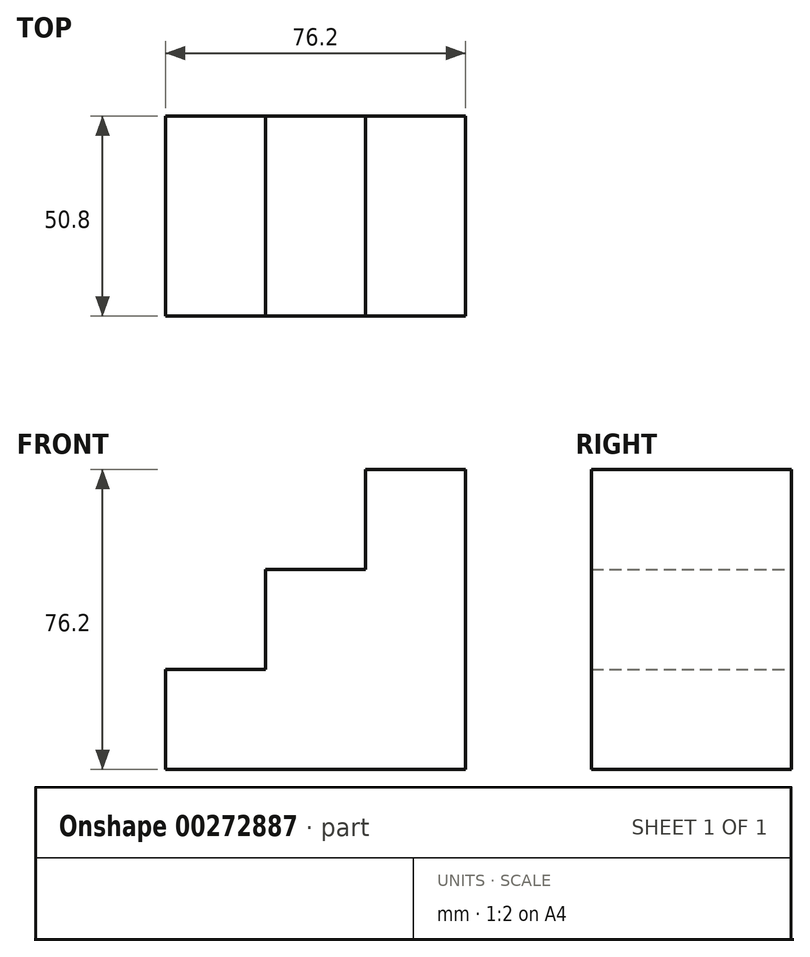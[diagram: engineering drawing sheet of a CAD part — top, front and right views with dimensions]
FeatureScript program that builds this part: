
annotation { "Feature Type Name" : "Feature", "Feature Type Description" : "" }
export const myFeature = defineFeature(function(context is Context, id is Id, definition is map)
    precondition{}
    {
        {
            var Q0;
            Q0=qCreatedBy(makeId("Front.planeOp"),FACE);
            var sketch = newSketch(context, id + "F0", { "sketchPlane" : qUnion([Q0])});
            skLineSegment(sketch, "E0", {"start": v(0, 0) * mm, "end": v(0, 76.2) * mm});
            skLineSegment(sketch, "E1", {"start": v(0, 76.2) * mm, "end": v(-25.4, 76.2) * mm});
            skLineSegment(sketch, "E2", {"start": v(-25.4, 76.2) * mm, "end": v(-25.4, 50.8) * mm});
            skLineSegment(sketch, "E3", {"start": v(-25.4, 50.8) * mm, "end": v(-50.8, 50.8) * mm});
            skLineSegment(sketch, "E4", {"start": v(-50.8, 50.8) * mm, "end": v(-50.8, 25.4) * mm});
            skLineSegment(sketch, "E5", {"start": v(-50.8, 25.4) * mm, "end": v(-76.2, 25.4) * mm});
            skLineSegment(sketch, "E6", {"start": v(-76.2, 25.4) * mm, "end": v(-76.2, 0) * mm});
            skLineSegment(sketch, "E7", {"start": v(-76.2, 0) * mm, "end": v(0, 0) * mm});
            skSolve(sketch);
        }
        {
            var Q0;
            Q0 = qSketchRegion(id + "F0", true);
            extrude(context, id + "F1", {"entities" : qUnion([Q0]), "depth" : 50.8 * mm});
        }
    });
